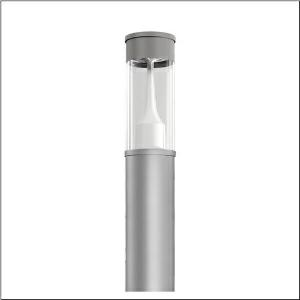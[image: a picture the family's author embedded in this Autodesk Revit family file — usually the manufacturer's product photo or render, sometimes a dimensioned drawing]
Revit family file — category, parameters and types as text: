
# Revit family: city-light_400_iq___p1_0a_5xa5305ff14hp_6c14
name_source: partatom
category: Lighting Fixtures
units: mm (PartAtom-declared; Revit-internal decimal feet)

## family parameters
Cut with Voids When Loaded = No
Host = Face
Light Source = No
Part Type = Normal
Room Calculation Point = No
Round Connector Dimension = Use Diameter
Shared = No

## types (1)
- --- (1 x LED, 4700 lm, 33.6 W, 3000K)
    Apparent Load = 34 VA
    CIE Flux Codes = 31 62 91 95 100
    Color Rendering = 70
    Color Temperature = 3000K
    Default Elevation = 1800 mm
    Description = City-Light 400 iQ, light pillar, Module 540 iQ-SR, primary light control with 3 zone facetted reflector, of plastic, silver coated, highly specular, structured, primary optical cover: cover, of PMMA, transparent, partly coated, light distribution: P1.0a, primary light characteristic: strongly asymmetric, LED, High Power LED, rated luminous flux: 4.700lm, luminous efficacy: 140lm/W, light colour: 730, colour temperature: 3000K, control gear: ECG iQ, control: pre-setting: logarithmic dimming characteristic, Street-Remote, Auto-Match, Temp-Guard, Lumen-Switch, Night-Set, Smart-Wire, Light-Fading, Desk-Remote (wireless, voltage-free reading and setting of iQ features in the workshop via application-optimized NFC function/RFID function), optimised constant luminous flux control (CLO 2.0), with terminal, 6-pole, max. 2.5mm², mains connection: 230..240V, AC, 50/60Hz, start of lifetime: 34W, end of service life: 36W, reduction: 15W, luminaire housing, cylindrical, of extruded aluminium section, coated, Siteco® metallic grey (DB 702S), length: 4.694mm, diameter: 200mm, Module 540 iQ-SR, traffic white (RAL 9016), equipment: Power, protection rating (complete): IP65, insulation class (complete): insulation class II (safety insulation), certification: CE, ENEC, VDE, packaging unit: 1 piece

Light Distribution: P1.0a
    Height = 500 mm
    Lamp = 1 x LED
    Lamp Light Flux = 4700 lm
    Lamp Power = 33.6 W
    Lamp count = 1
    Length = 200 mm  [stored 0.656168 ft]
    Luminous efficacy = 140 lm/W
    Manufacturer = Siteco
    ModVariant = No
    Model = 5XA5305FF14HP
    Mounting Place = Floor
    Mounting Type = Freestanding
    Number of Poles = 1
    OnlyDefault = Yes
    Power Factor = 1
    Product Name = City-Light 400 iQ | P1.0a
    Product group = light pillar
    ProductGroupID = 1301
    Protection Class = Protection class II
    Protection Degree = IP 65
    RLX_Detail_Level = 1
    RLX_Emergency_Light_Flux = 0 lm
    RLX_Emergency_Type = 0
    RLX_Emergency_Type_DB = No
    RlxData = <blob elided: 53317 chars, md5=4a6e961d>
    Socket = socket
    Standby Power = 0 W
    System Light Flux = 4700 lm
    System Power = 34 W
    Type Comments = factory setting: luminous flux: 100 % | dim-lin: 254 | 695 mA
    Type Image = l_1006916.jpg
    URL = http://relux.com
    VarID = @adj_165431
    Voltage = 0 V
    Weight = 0.00 kg
    Width = 0 mm  [stored 0 ft]

note: [stored X ft] marks values corroborated as IEEE doubles in the binary element streams (Revit-internal decimal feet)

## geometry (parser evidence)
native form markers: Blend x4, Sweep x11
no freeform markers — native parametric forms only
